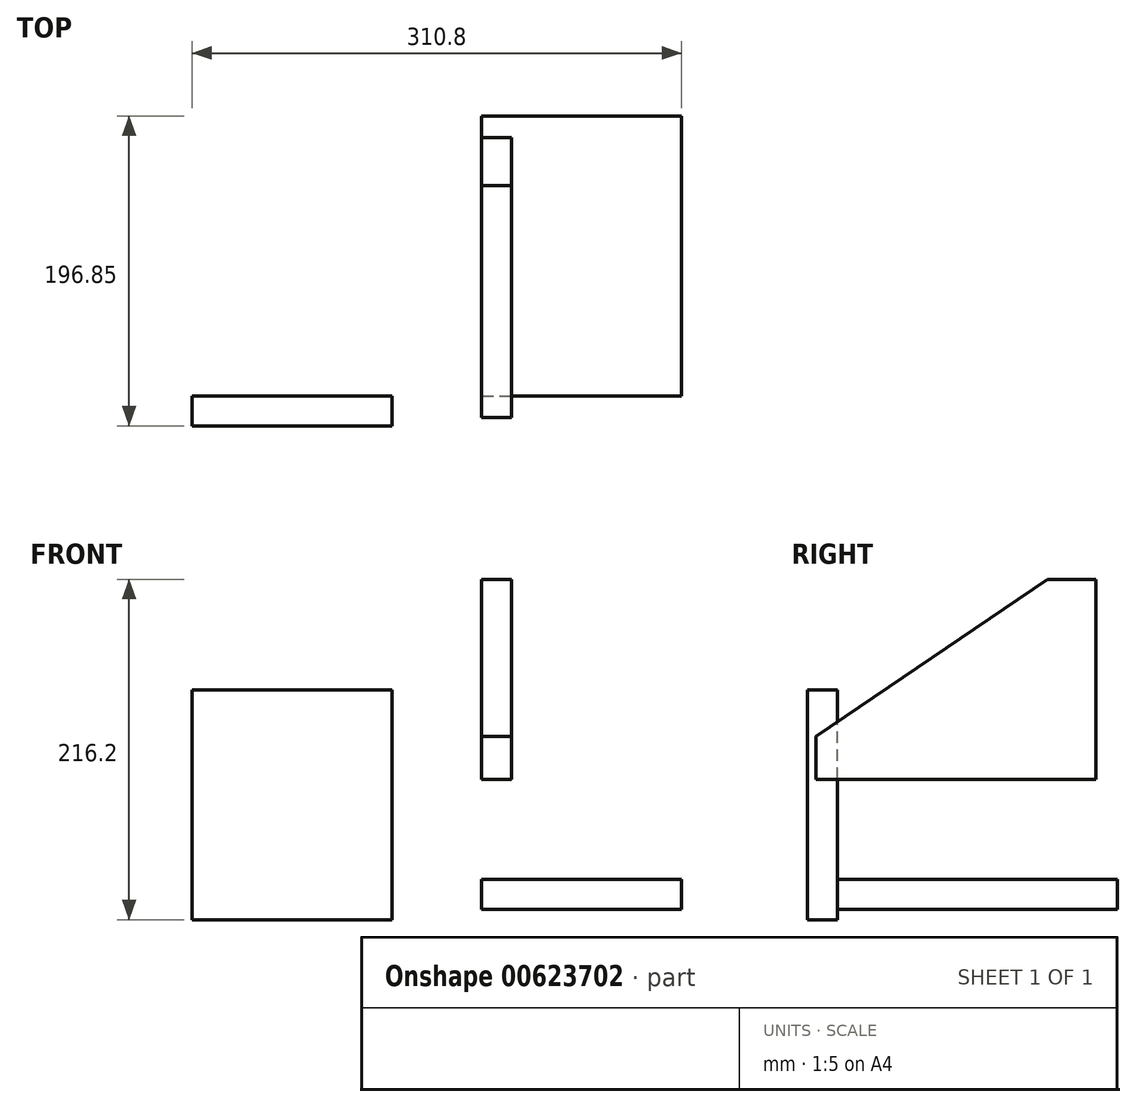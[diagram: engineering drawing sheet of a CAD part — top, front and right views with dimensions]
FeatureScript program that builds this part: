
annotation { "Feature Type Name" : "Feature", "Feature Type Description" : "" }
export const myFeature = defineFeature(function(context is Context, id is Id, definition is map)
    precondition{}
    {
        {
            var Q0;
            Q0=qCreatedBy(makeId("Top.planeOp"),FACE);
            var sketch = newSketch(context, id + "F0", { "sketchPlane" : qUnion([Q0])});
            skLineSegment(sketch, "E0.bottom", {"start": v(0, 0) * mm, "end": v(127, 0) * mm});
            skLineSegment(sketch, "E0.top", {"start": v(0, 177.8) * mm, "end": v(127, 177.8) * mm});
            skLineSegment(sketch, "E0.left", {"start": v(0, 0) * mm, "end": v(0, 177.8) * mm});
            skLineSegment(sketch, "E0.right", {"start": v(127, 0) * mm, "end": v(127, 177.8) * mm});
            skSolve(sketch);
        }
        {
            var Q0;
            Q0=makeQuery(id+"F0.imprint","IMPRINT",FACE,{"disambiguationData":[TD([[makeQuery(id+"F0.imprint","IMPRINT",EDGE,{"derivedFrom":sQuery(id+"F0.wireOp",EDGE,"E0.bottom")}),1.0]])]});
            extrude(context, id + "F1", {"entities" : qUnion([Q0]), "oppositeDirection" : true, "depth" : 19.05 * mm, "offsetDistance" : 25.4 * mm});
        }
        {
            var Q0;
            Q0=qCreatedBy(makeId("Right.planeOp"),FACE);
            var sketch = newSketch(context, id + "F2", { "sketchPlane" : qUnion([Q0])});
            skLineSegment(sketch, "E1.bottom", {"start": v(-13.7, 63.57) * mm, "end": v(164.1, 63.57) * mm});
            skLineSegment(sketch, "E1.top", {"start": v(-13.7, 190.57) * mm, "end": v(164.1, 190.57) * mm});
            skLineSegment(sketch, "E1.left", {"start": v(-13.7, 63.57) * mm, "end": v(-13.7, 190.57) * mm});
            skLineSegment(sketch, "E1.right", {"start": v(164.1, 63.57) * mm, "end": v(164.1, 190.57) * mm});
            skSolve(sketch);
        }
        {
            var Q0;
            Q0 = qSketchRegion(id + "F2", true);
            extrude(context, id + "F3", {"entities" : qUnion([Q0]), "operationType" : NewBodyOperationType.ADD, "depth" : 19.05 * mm, "offsetDistance" : 25.4 * mm});
        }
        {
            var Q0;
            Q0=makeQuery(id+"F3.opExtrude","CAP_FACE",FACE,{"disambiguationData":[OSD([sQuery(id+"F2.wireOp",EDGE,"E1.bottom"),sQuery(id+"F2.wireOp",EDGE,"E1.top"),sQuery(id+"F2.wireOp",EDGE,"E1.left"),sQuery(id+"F2.wireOp",EDGE,"E1.right")])],"isStart":false});
            var sketch = newSketch(context, id + "F4", { "sketchPlane" : qUnion([Q0])});
            skLineSegment(sketch, "E2", {"start": v(86.7, 190.57) * mm, "end": v(-13.7, 124.18) * mm});
            skSolve(sketch);
        }
        {
            var Q0;
            {var subQ0=sQuery(id+"F4.wireOp",EDGE,"E2");Q0=makeQuery(id+"F4.imprint","IMPRINT",FACE,{"disambiguationData":[TD([[makeQuery(id+"F4.imprint","IMPRINT",EDGE,{"derivedFrom":subQ0}),-1.0]])]});}
            extrude(context, id + "F5", {"entities" : qUnion([Q0]), "operationType" : NewBodyOperationType.REMOVE, "oppositeDirection" : true, "depth" : 25.4 * mm, "offsetDistance" : 25.4 * mm});
        }
        {
            var Q0;
            Q0=makeQuery(id+"F3.opExtrude","CAP_FACE",FACE,{"disambiguationData":[OSD([sQuery(id+"F2.wireOp",EDGE,"E1.bottom"),sQuery(id+"F2.wireOp",EDGE,"E1.top"),sQuery(id+"F2.wireOp",EDGE,"E1.left"),sQuery(id+"F2.wireOp",EDGE,"E1.right")])],"isStart":false});
            var sketch = newSketch(context, id + "F6", { "sketchPlane" : qUnion([Q0])});
            skLineSegment(sketch, "E3", {"start": v(133.38, 190.57) * mm, "end": v(-13.7, 90.73) * mm});
            skSolve(sketch);
        }
        {
            var Q0;
            {var subQ0=sQuery(id+"F6.wireOp",EDGE,"E3");Q0=makeQuery(id+"F6.imprint","IMPRINT",FACE,{"disambiguationData":[TD([[makeQuery(id+"F6.imprint","IMPRINT",EDGE,{"derivedFrom":subQ0}),-1.0]])]});}
            extrude(context, id + "F7", {"entities" : qUnion([Q0]), "operationType" : NewBodyOperationType.REMOVE, "oppositeDirection" : true, "depth" : 25.4 * mm, "offsetDistance" : 25.4 * mm});
        }
        {
            var Q0;
            Q0=qCreatedBy(makeId("Front.planeOp"),FACE);
            var sketch = newSketch(context, id + "F8", { "sketchPlane" : qUnion([Q0])});
            skLineSegment(sketch, "E4.bottom", {"start": v(-183.8, -25.63) * mm, "end": v(-56.8, -25.63) * mm});
            skLineSegment(sketch, "E4.top", {"start": v(-183.8, 120.42) * mm, "end": v(-56.8, 120.42) * mm});
            skLineSegment(sketch, "E4.left", {"start": v(-183.8, -25.63) * mm, "end": v(-183.8, 120.42) * mm});
            skLineSegment(sketch, "E4.right", {"start": v(-56.8, -25.63) * mm, "end": v(-56.8, 120.42) * mm});
            skSolve(sketch);
        }
        {
            var Q0;
            Q0=makeQuery(id+"F8.imprint","IMPRINT",FACE,{"disambiguationData":[TD([[makeQuery(id+"F8.imprint","IMPRINT",EDGE,{"derivedFrom":sQuery(id+"F8.wireOp",EDGE,"E4.bottom")}),1.0]])]});
            extrude(context, id + "F9", {"entities" : qUnion([Q0]), "depth" : 19.05 * mm, "offsetDistance" : 25.4 * mm});
        }
    });
